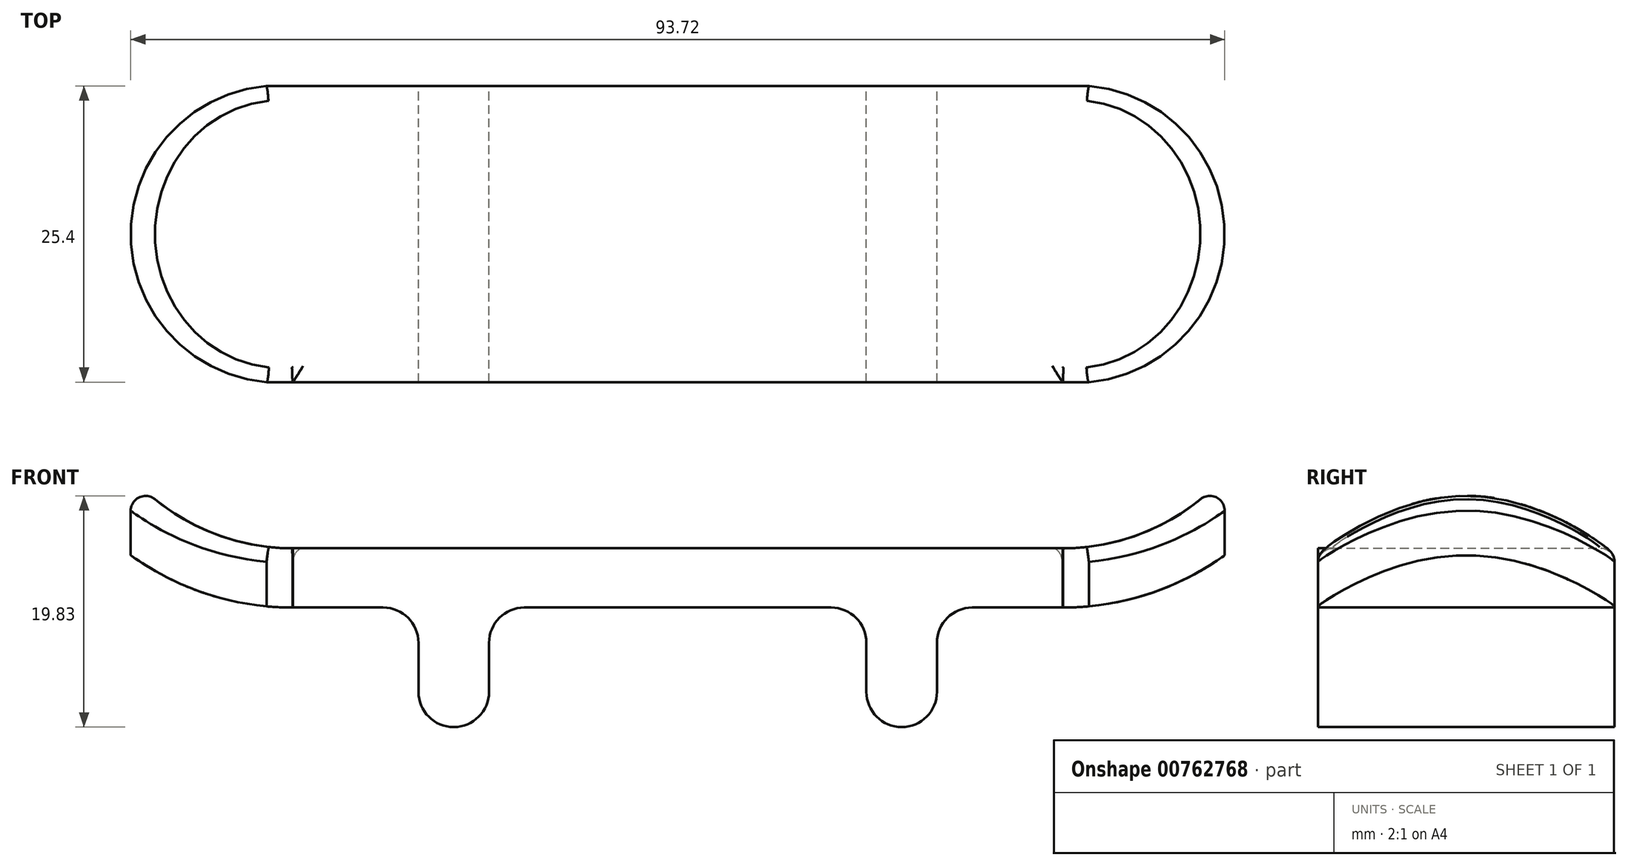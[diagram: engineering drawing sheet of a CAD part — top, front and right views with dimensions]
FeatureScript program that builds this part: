
annotation { "Feature Type Name" : "Feature", "Feature Type Description" : "" }
export const myFeature = defineFeature(function(context is Context, id is Id, definition is map)
    precondition{}
    {
        {
            var Q0;
            Q0=qCreatedBy(makeId("Front.planeOp"),FACE);
            var sketch = newSketch(context, id + "F0", { "sketchPlane" : qUnion([Q0])});
            skArc(sketch, "E0", {"start": v(-47.36, 9.42) * mm, "mid": v(-40.93, 4.43) * mm, "end": v(-32.98, 2.65) * mm});
            skArc(sketch, "E1.0", {"start": v(-51.28, 6.18) * mm, "mid": v(-43.09, -0.17) * mm, "end": v(-32.98, -2.43) * mm});
            skArc(sketch, "E2", {"start": v(-47.36, 9.42) * mm, "mid": v(-50.92, 9.73) * mm, "end": v(-51.28, 6.18) * mm});
            skArc(sketch, "E3.MirrorCS", {"start": v(51.28, 6.18) * mm, "mid": v(43.09, -0.17) * mm, "end": v(32.98, -2.43) * mm});
            skArc(sketch, "E4.MirrorCS", {"start": v(47.36, 9.42) * mm, "mid": v(50.92, 9.73) * mm, "end": v(51.28, 6.18) * mm});
            skArc(sketch, "E5.MirrorCS", {"start": v(47.36, 9.42) * mm, "mid": v(40.93, 4.43) * mm, "end": v(32.98, 2.65) * mm});
            skLineSegment(sketch, "E6", {"start": v(32.98, 2.65) * mm, "end": v(-32.98, 2.65) * mm});
            skLineSegment(sketch, "E7", {"start": v(-32.98, -2.43) * mm, "end": v(32.98, -2.43) * mm});
            skSolve(sketch);
        }
        {
            var Q0;
            Q0 = qSketchRegion(id + "F0", true);
            extrude(context, id + "F1", {"entities" : qUnion([Q0]), "endBound" : BoundingType.SYMMETRIC, "depth" : 25.4 * mm, "offsetDistance" : 25.4 * mm});
        }
        {
            var Q0;
            Q0=qCreatedBy(makeId("Top.planeOp"),FACE);
            var sketch = newSketch(context, id + "F2", { "sketchPlane" : qUnion([Q0])});
            skLineSegment(sketch, "E8", {"start": v(0, -14.58) * mm, "end": v(0, 29.55) * mm, "construction": true});
            skArc(sketch, "E9", {"start": v(-32.98, 12.7) * mm, "mid": v(-46.86, 0) * mm, "end": v(-32.97, -12.7) * mm});
            skArc(sketch, "E10", {"start": v(-32.98, 12.7) * mm, "mid": v(-74.18, 0) * mm, "end": v(-32.97, -12.7) * mm});
            skArc(sketch, "E11.MirrorCS", {"start": v(32.98, 12.7) * mm, "mid": v(46.86, 0) * mm, "end": v(32.97, -12.7) * mm});
            skArc(sketch, "E12.MirrorCS", {"start": v(32.98, 12.7) * mm, "mid": v(74.18, 0) * mm, "end": v(32.97, -12.7) * mm});
            skSolve(sketch);
        }
        {
            var Q0;
            Q0 = qSketchRegion(id + "F2", true);
            extrude(context, id + "F3", {"entities" : qUnion([Q0]), "operationType" : NewBodyOperationType.REMOVE, "endBound" : BoundingType.SYMMETRIC, "depth" : 254 * mm, "offsetDistance" : 25.4 * mm});
        }
        {
            var Q0;
            Q0=qCreatedBy(makeId("Front.planeOp"),FACE);
            var sketch = newSketch(context, id + "F4", { "sketchPlane" : qUnion([Q0])});
            skLineSegment(sketch, "E13.bottom", {"start": v(-22.21, 0) * mm, "end": v(-16.16, 0) * mm});
            skLineSegment(sketch, "E13.top", {"start": v(-22.21, -12.68) * mm, "end": v(-16.16, -12.68) * mm});
            skLineSegment(sketch, "E13.left", {"start": v(-22.21, 0) * mm, "end": v(-22.21, -12.68) * mm});
            skLineSegment(sketch, "E13.right", {"start": v(-16.16, 0) * mm, "end": v(-16.16, -12.68) * mm});
            skLineSegment(sketch, "E14", {"start": v(0, -20.12) * mm, "end": v(0, 21.05) * mm, "construction": true});
            skLineSegment(sketch, "E15.MirrorCS", {"start": v(16.16, 0) * mm, "end": v(16.16, -12.68) * mm});
            skLineSegment(sketch, "E16.MirrorCS", {"start": v(22.21, 0) * mm, "end": v(22.21, -12.68) * mm});
            skLineSegment(sketch, "E17.MirrorCS", {"start": v(22.21, -12.68) * mm, "end": v(16.16, -12.68) * mm});
            skLineSegment(sketch, "E18.MirrorCS", {"start": v(22.21, 0) * mm, "end": v(16.16, 0) * mm});
            skSolve(sketch);
        }
        {
            var Q0;
            Q0 = qSketchRegion(id + "F4", true);
            extrude(context, id + "F5", {"entities" : qUnion([Q0]), "operationType" : NewBodyOperationType.ADD, "endBound" : BoundingType.SYMMETRIC, "depth" : 25.4 * mm, "offsetDistance" : 25.4 * mm});
        }
        {
            var Q0;
            Q0=makeQuery(id+"F5.opExtrude","SWEPT_EDGE",EDGE,{"disambiguationData":[OSD([sQuery(id+"F4.wireOp",EDGE,"E13.top"),sQuery(id+"F4.wireOp",EDGE,"E13.left")])]});
            var Q1;
            Q1=makeQuery(id+"F5.opExtrude","SWEPT_EDGE",EDGE,{"disambiguationData":[OSD([sQuery(id+"F4.wireOp",EDGE,"E13.top"),sQuery(id+"F4.wireOp",EDGE,"E13.right")])]});
            var Q2;
            Q2=makeQuery(id+"F5.opExtrude","SWEPT_EDGE",EDGE,{"disambiguationData":[OSD([sQuery(id+"F4.wireOp",EDGE,"E15.MirrorCS"),sQuery(id+"F4.wireOp",EDGE,"E17.MirrorCS")])]});
            var Q3;
            Q3=makeQuery(id+"F5.opExtrude","SWEPT_EDGE",EDGE,{"disambiguationData":[OSD([sQuery(id+"F4.wireOp",EDGE,"E16.MirrorCS"),sQuery(id+"F4.wireOp",EDGE,"E17.MirrorCS")])]});
            var Q4;
            Q4=makeQuery(id+"F5.boolean.opBoolean","INTERSECT",EDGE,{"derivedFrom":[makeQuery(id+"F1.opExtrude","SWEPT_FACE",FACE,{"disambiguationData":[OSD([sQuery(id+"F0.wireOp",EDGE,"E7")])]}),makeQuery(id+"F5.opExtrude","SWEPT_FACE",FACE,{"disambiguationData":[OSD([sQuery(id+"F4.wireOp",EDGE,"E13.right")])]})]});
            var Q5;
            Q5=makeQuery(id+"F5.boolean.opBoolean","INTERSECT",EDGE,{"derivedFrom":[makeQuery(id+"F1.opExtrude","SWEPT_FACE",FACE,{"disambiguationData":[OSD([sQuery(id+"F0.wireOp",EDGE,"E7")])]}),makeQuery(id+"F5.opExtrude","SWEPT_FACE",FACE,{"disambiguationData":[OSD([sQuery(id+"F4.wireOp",EDGE,"E13.left")])]})]});
            var Q6;
            Q6=makeQuery(id+"F5.boolean.opBoolean","INTERSECT",EDGE,{"derivedFrom":[makeQuery(id+"F1.opExtrude","SWEPT_FACE",FACE,{"disambiguationData":[OSD([sQuery(id+"F0.wireOp",EDGE,"E7")])]}),makeQuery(id+"F5.opExtrude","SWEPT_FACE",FACE,{"disambiguationData":[OSD([sQuery(id+"F4.wireOp",EDGE,"E15.MirrorCS")])]})]});
            var Q7;
            Q7=makeQuery(id+"F5.boolean.opBoolean","INTERSECT",EDGE,{"derivedFrom":[makeQuery(id+"F1.opExtrude","SWEPT_FACE",FACE,{"disambiguationData":[OSD([sQuery(id+"F0.wireOp",EDGE,"E7")])]}),makeQuery(id+"F5.opExtrude","SWEPT_FACE",FACE,{"disambiguationData":[OSD([sQuery(id+"F4.wireOp",EDGE,"E16.MirrorCS")])]})]});
            fillet(context, id + "F6", {"entities" : qUnion([Q0, Q1, Q2, Q3, Q4, Q5, Q6, Q7]), "tangentPropagation" : true, "radius" : 3.02 * mm, "defaultsChanged" : false, "vertexSettings" : [], "allowEdgeOverflow" : false});
        }
        {
            var Q0;
            Q0=makeQuery(id+"F3.boolean.opBoolean","INTERSECT",EDGE,{"disambiguationData":[OD(1.0)],"derivedFrom":[makeQuery(id+"F1.opExtrude","SWEPT_FACE",FACE,{"disambiguationData":[OSD([sQuery(id+"F0.wireOp",EDGE,"E0")])]}),makeQuery(id+"F3.opExtrude","SWEPT_FACE",FACE,{"disambiguationData":[OSD([sQuery(id+"F2.wireOp",EDGE,"E9")])]})]});
            var Q1;
            Q1=makeQuery(id+"F1.opExtrude","CAP_EDGE",EDGE,{"disambiguationData":[OSD([sQuery(id+"F0.wireOp",EDGE,"E0")])],"isStart":false});
            var Q2;
            Q2=makeQuery(id+"F1.opExtrude","CAP_EDGE",EDGE,{"disambiguationData":[OSD([sQuery(id+"F0.wireOp",EDGE,"E0")])],"isStart":true});
            var Q3;
            Q3=makeQuery(id+"F3.boolean.opBoolean","INTERSECT",EDGE,{"disambiguationData":[OD(1.0)],"derivedFrom":[makeQuery(id+"F1.opExtrude","SWEPT_FACE",FACE,{"disambiguationData":[OSD([sQuery(id+"F0.wireOp",EDGE,"E5.MirrorCS")])]}),makeQuery(id+"F3.opExtrude","SWEPT_FACE",FACE,{"disambiguationData":[OSD([sQuery(id+"F2.wireOp",EDGE,"E11.MirrorCS")])]})]});
            var Q4;
            Q4=makeQuery(id+"F1.opExtrude","CAP_EDGE",EDGE,{"disambiguationData":[OSD([sQuery(id+"F0.wireOp",EDGE,"E5.MirrorCS")])],"isStart":true});
            var Q5;
            Q5=makeQuery(id+"F1.opExtrude","CAP_EDGE",EDGE,{"disambiguationData":[OSD([sQuery(id+"F0.wireOp",EDGE,"E5.MirrorCS")])],"isStart":false});
            fillet(context, id + "F7", {"entities" : qUnion([Q0, Q1, Q2, Q3, Q4, Q5]), "tangentPropagation" : true, "radius" : 1.27 * mm, "defaultsChanged" : false, "vertexSettings" : [], "allowEdgeOverflow" : false});
        }
    });
